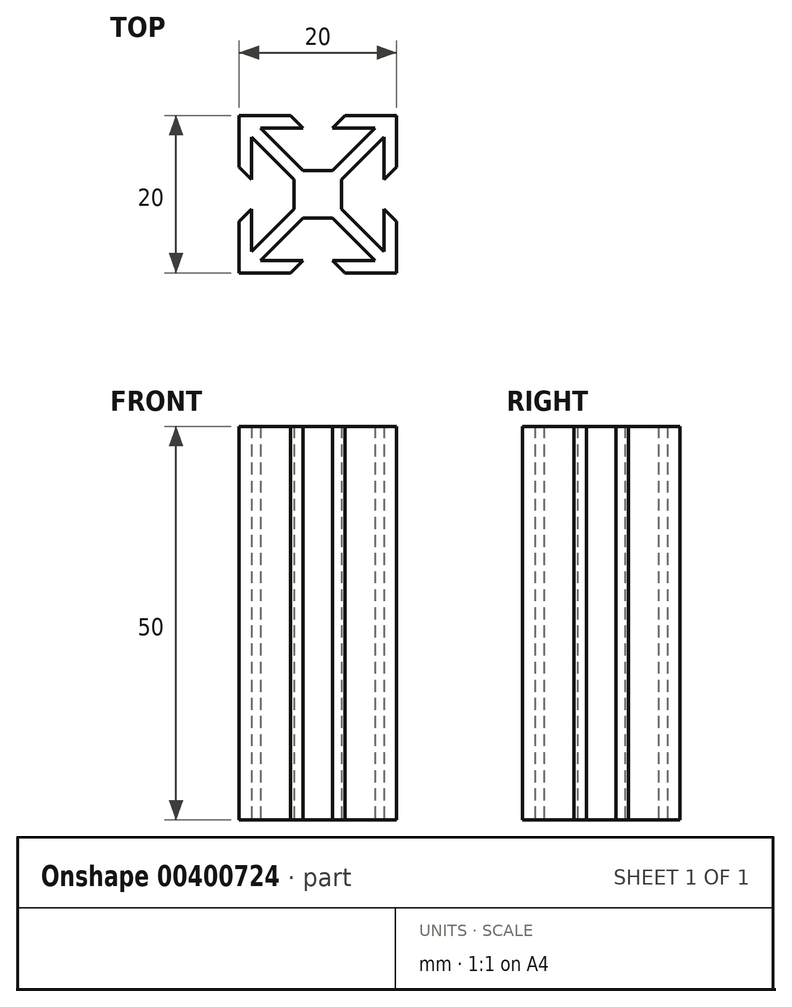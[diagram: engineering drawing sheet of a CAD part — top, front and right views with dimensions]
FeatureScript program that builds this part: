
annotation { "Feature Type Name" : "Feature", "Feature Type Description" : "" }
export const myFeature = defineFeature(function(context is Context, id is Id, definition is map)
    precondition{}
    {
        {
            var Q0;
            Q0=qCreatedBy(makeId("Top.planeOp"),FACE);
            var sketch = newSketch(context, id + "F0", { "sketchPlane" : qUnion([Q0])});
            skLineSegment(sketch, "E0.bottom", {"start": v(-10, 10) * mm, "end": v(10, 10) * mm});
            skLineSegment(sketch, "E0.top", {"start": v(-10, -10) * mm, "end": v(10, -10) * mm});
            skLineSegment(sketch, "E0.left", {"start": v(-10, 10) * mm, "end": v(-10, -10) * mm});
            skLineSegment(sketch, "E0.right", {"start": v(10, 10) * mm, "end": v(10, -10) * mm});
            skPoint(sketch, "E0.middle", {"position": v(0, 0) * mm});
            skLineSegment(sketch, "E1.bottom", {"start": v(3, -3) * mm, "end": v(-3, -3) * mm});
            skLineSegment(sketch, "E1.top", {"start": v(3, 3) * mm, "end": v(-3, 3) * mm});
            skLineSegment(sketch, "E1.left", {"start": v(3, -3) * mm, "end": v(3, 3) * mm});
            skLineSegment(sketch, "E1.right", {"start": v(-3, -3) * mm, "end": v(-3, 3) * mm});
            skLineSegment(sketch, "E2", {"start": v(-3, -1.87) * mm, "end": v(-1.87, -3) * mm});
            skLineSegment(sketch, "E3", {"start": v(1.87, -3) * mm, "end": v(3, -1.87) * mm});
            skLineSegment(sketch, "E4", {"start": v(1.87, 3) * mm, "end": v(3, 1.87) * mm});
            skLineSegment(sketch, "E5", {"start": v(-3, 1.87) * mm, "end": v(-1.87, 3) * mm});
            skLineSegment(sketch, "E6", {"start": v(-1.87, -3) * mm, "end": v(-8.87, -10) * mm});
            skLineSegment(sketch, "E7", {"start": v(-3, -1.87) * mm, "end": v(-10, -8.87) * mm});
            skLineSegment(sketch, "E8", {"start": v(-3, 1.87) * mm, "end": v(-10, 8.87) * mm});
            skLineSegment(sketch, "E9", {"start": v(-1.87, 3) * mm, "end": v(-8.87, 10) * mm});
            skLineSegment(sketch, "E10", {"start": v(1.87, 3) * mm, "end": v(8.87, 10) * mm});
            skLineSegment(sketch, "E11", {"start": v(3, 1.87) * mm, "end": v(10, 8.87) * mm});
            skLineSegment(sketch, "E12", {"start": v(3, -1.87) * mm, "end": v(10, -8.87) * mm});
            skLineSegment(sketch, "E13", {"start": v(1.87, -3) * mm, "end": v(8.87, -10) * mm});
            skLineSegment(sketch, "E14", {"start": v(-1.87, -8.4) * mm, "end": v(-7.27, -8.4) * mm});
            skLineSegment(sketch, "E15", {"start": v(-1.87, -8.4) * mm, "end": v(-3.47, -10) * mm});
            skLineSegment(sketch, "E16", {"start": v(1.87, -8.4) * mm, "end": v(7.27, -8.4) * mm});
            skLineSegment(sketch, "E17", {"start": v(1.87, -8.4) * mm, "end": v(3.47, -10) * mm});
            skLineSegment(sketch, "E18", {"start": v(10, -3.47) * mm, "end": v(8.4, -1.87) * mm});
            skLineSegment(sketch, "E19", {"start": v(8.4, -1.87) * mm, "end": v(8.4, -7.27) * mm});
            skLineSegment(sketch, "E20", {"start": v(10, 3.47) * mm, "end": v(8.4, 1.87) * mm});
            skLineSegment(sketch, "E21", {"start": v(8.4, 1.87) * mm, "end": v(8.4, 7.27) * mm});
            skLineSegment(sketch, "E22", {"start": v(3.47, 10) * mm, "end": v(1.87, 8.4) * mm});
            skLineSegment(sketch, "E23", {"start": v(1.87, 8.4) * mm, "end": v(7.27, 8.4) * mm});
            skLineSegment(sketch, "E24", {"start": v(-3.47, 10) * mm, "end": v(-1.87, 8.4) * mm});
            skLineSegment(sketch, "E25", {"start": v(-1.87, 8.4) * mm, "end": v(-7.27, 8.4) * mm});
            skLineSegment(sketch, "E26", {"start": v(-10, 3.47) * mm, "end": v(-8.4, 1.87) * mm});
            skLineSegment(sketch, "E27", {"start": v(-8.4, 1.87) * mm, "end": v(-8.4, 7.27) * mm});
            skLineSegment(sketch, "E28", {"start": v(-10, -3.47) * mm, "end": v(-8.4, -1.87) * mm});
            skLineSegment(sketch, "E29", {"start": v(-8.4, -1.87) * mm, "end": v(-8.4, -7.27) * mm});
            skSolve(sketch);
        }
        {
            var Q0;
            {var subQ8=sQuery(id+"F0.wireOp",EDGE,"E0.left");var subQ9=sQuery(id+"F0.wireOp",EDGE,"E0.top");var subQ10=makeQuery(id+"F0.imprint","INTERSECT",VERTEX,{"derivedFrom":[subQ9,subQ8]});Q0=makeQuery(id+"F0.imprint","IMPRINT",FACE,{"disambiguationData":[TD([[makeQuery(id+"F0.imprint","IMPRINT",EDGE,{"disambiguationData":[TD([[subQ10,-1.0]])],"derivedFrom":subQ9}),1.0]])]});}
            var Q1;
            {var subQ4=sQuery(id+"F0.wireOp",EDGE,"E14");Q1=makeQuery(id+"F0.imprint","IMPRINT",FACE,{"disambiguationData":[TD([[makeQuery(id+"F0.imprint","IMPRINT",EDGE,{"derivedFrom":subQ4}),1.0]])]});}
            var Q2;
            {var subQ3=sQuery(id+"F0.wireOp",EDGE,"E28");Q2=makeQuery(id+"F0.imprint","IMPRINT",FACE,{"disambiguationData":[TD([[makeQuery(id+"F0.imprint","IMPRINT",EDGE,{"derivedFrom":subQ3}),-1.0]])]});}
            var Q3;
            {var subQ0=sQuery(id+"F0.wireOp",EDGE,"E2");Q3=makeQuery(id+"F0.imprint","IMPRINT",FACE,{"disambiguationData":[TD([[makeQuery(id+"F0.imprint","IMPRINT",EDGE,{"derivedFrom":subQ0}),1.0]])]});}
            var Q4;
            {var subQ3=sQuery(id+"F0.wireOp",EDGE,"E2");Q4=makeQuery(id+"F0.imprint","IMPRINT",FACE,{"disambiguationData":[TD([[makeQuery(id+"F0.imprint","IMPRINT",EDGE,{"derivedFrom":subQ3}),-1.0]])]});}
            var Q5;
            {var subQ3=sQuery(id+"F0.wireOp",EDGE,"E3");Q5=makeQuery(id+"F0.imprint","IMPRINT",FACE,{"disambiguationData":[TD([[makeQuery(id+"F0.imprint","IMPRINT",EDGE,{"derivedFrom":subQ3}),-1.0]])]});}
            var Q6;
            {var subQ9=sQuery(id+"F0.wireOp",EDGE,"E0.right");var subQ10=sQuery(id+"F0.wireOp",EDGE,"E0.top");var subQ11=makeQuery(id+"F0.imprint","INTERSECT",VERTEX,{"derivedFrom":[subQ10,subQ9]});Q6=makeQuery(id+"F0.imprint","IMPRINT",FACE,{"disambiguationData":[TD([[makeQuery(id+"F0.imprint","IMPRINT",EDGE,{"disambiguationData":[TD([[subQ11,1.0]])],"derivedFrom":subQ10}),1.0]])]});}
            var Q7;
            {var subQ4=sQuery(id+"F0.wireOp",EDGE,"E16");Q7=makeQuery(id+"F0.imprint","IMPRINT",FACE,{"disambiguationData":[TD([[makeQuery(id+"F0.imprint","IMPRINT",EDGE,{"derivedFrom":subQ4}),-1.0]])]});}
            var Q8;
            {var subQ3=sQuery(id+"F0.wireOp",EDGE,"E18");Q8=makeQuery(id+"F0.imprint","IMPRINT",FACE,{"disambiguationData":[TD([[makeQuery(id+"F0.imprint","IMPRINT",EDGE,{"derivedFrom":subQ3}),1.0]])]});}
            var Q9;
            {var subQ3=sQuery(id+"F0.wireOp",EDGE,"E20");Q9=makeQuery(id+"F0.imprint","IMPRINT",FACE,{"disambiguationData":[TD([[makeQuery(id+"F0.imprint","IMPRINT",EDGE,{"derivedFrom":subQ3}),-1.0]])]});}
            var Q10;
            {var subQ8=sQuery(id+"F0.wireOp",EDGE,"E0.bottom");var subQ11=sQuery(id+"F0.wireOp",EDGE,"E0.right");var subQ12=makeQuery(id+"F0.imprint","INTERSECT",VERTEX,{"derivedFrom":[subQ8,subQ11]});Q10=makeQuery(id+"F0.imprint","IMPRINT",FACE,{"disambiguationData":[TD([[makeQuery(id+"F0.imprint","IMPRINT",EDGE,{"disambiguationData":[TD([[subQ12,1.0]])],"derivedFrom":subQ8}),-1.0]])]});}
            var Q11;
            {var subQ3=sQuery(id+"F0.wireOp",EDGE,"E22");Q11=makeQuery(id+"F0.imprint","IMPRINT",FACE,{"disambiguationData":[TD([[makeQuery(id+"F0.imprint","IMPRINT",EDGE,{"derivedFrom":subQ3}),1.0]])]});}
            var Q12;
            {var subQ3=sQuery(id+"F0.wireOp",EDGE,"E4");Q12=makeQuery(id+"F0.imprint","IMPRINT",FACE,{"disambiguationData":[TD([[makeQuery(id+"F0.imprint","IMPRINT",EDGE,{"derivedFrom":subQ3}),1.0]])]});}
            var Q13;
            {var subQ3=sQuery(id+"F0.wireOp",EDGE,"E5");Q13=makeQuery(id+"F0.imprint","IMPRINT",FACE,{"disambiguationData":[TD([[makeQuery(id+"F0.imprint","IMPRINT",EDGE,{"derivedFrom":subQ3}),1.0]])]});}
            var Q14;
            {var subQ9=sQuery(id+"F0.wireOp",EDGE,"E0.left");var subQ10=sQuery(id+"F0.wireOp",EDGE,"E0.bottom");var subQ11=makeQuery(id+"F0.imprint","INTERSECT",VERTEX,{"derivedFrom":[subQ10,subQ9]});Q14=makeQuery(id+"F0.imprint","IMPRINT",FACE,{"disambiguationData":[TD([[makeQuery(id+"F0.imprint","IMPRINT",EDGE,{"disambiguationData":[TD([[subQ11,-1.0]])],"derivedFrom":subQ10}),-1.0]])]});}
            var Q15;
            {var subQ3=sQuery(id+"F0.wireOp",EDGE,"E26");Q15=makeQuery(id+"F0.imprint","IMPRINT",FACE,{"disambiguationData":[TD([[makeQuery(id+"F0.imprint","IMPRINT",EDGE,{"derivedFrom":subQ3}),1.0]])]});}
            var Q16;
            {var subQ3=sQuery(id+"F0.wireOp",EDGE,"E24");Q16=makeQuery(id+"F0.imprint","IMPRINT",FACE,{"disambiguationData":[TD([[makeQuery(id+"F0.imprint","IMPRINT",EDGE,{"derivedFrom":subQ3}),-1.0]])]});}
            extrude(context, id + "F1", {"entities" : qUnion([Q0, Q1, Q2, Q3, Q4, Q5, Q6, Q7, Q8, Q9, Q10, Q11, Q12, Q13, Q14, Q15, Q16]), "depth" : 50 * mm});
        }
    });
